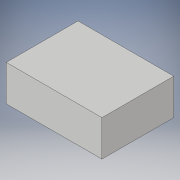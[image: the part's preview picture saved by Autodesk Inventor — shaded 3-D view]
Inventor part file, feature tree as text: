
AUTODESK INVENTOR PART (.ipt)
format: ipt  version: 2019 (Build 230136000, 136)  size: 108,032 bytes
history: native  units: in
note: dims shown in document units (in); Inventor stores cm internally (conversion verified against a paired STEP export)
features: extrude x2, sketch x2
ambient origin geometry x8: Origin, YZ Plane, XZ Plane, XY Plane, X Axis, Y Axis, Z Axis, Center Point
bodies: Solid1 (feature_tree)
feature tree (4):
  extrude  "Extrusion1"  Depth=6.0in
  extrude  "Extrusion2"  Depth=0.5in
  sketch  "Sketch1"  dims[d0=8.0in d1=6.0in]
  sketch  "Sketch2"  dims[d2=3.0in d3=0.0in d4=0.5in d5=0.5in d6=0.5in d7=0.5in d8=0.25in d9=0.25in d10=0.5in d11=0.5in d12=0.25in d13=0.0in]
